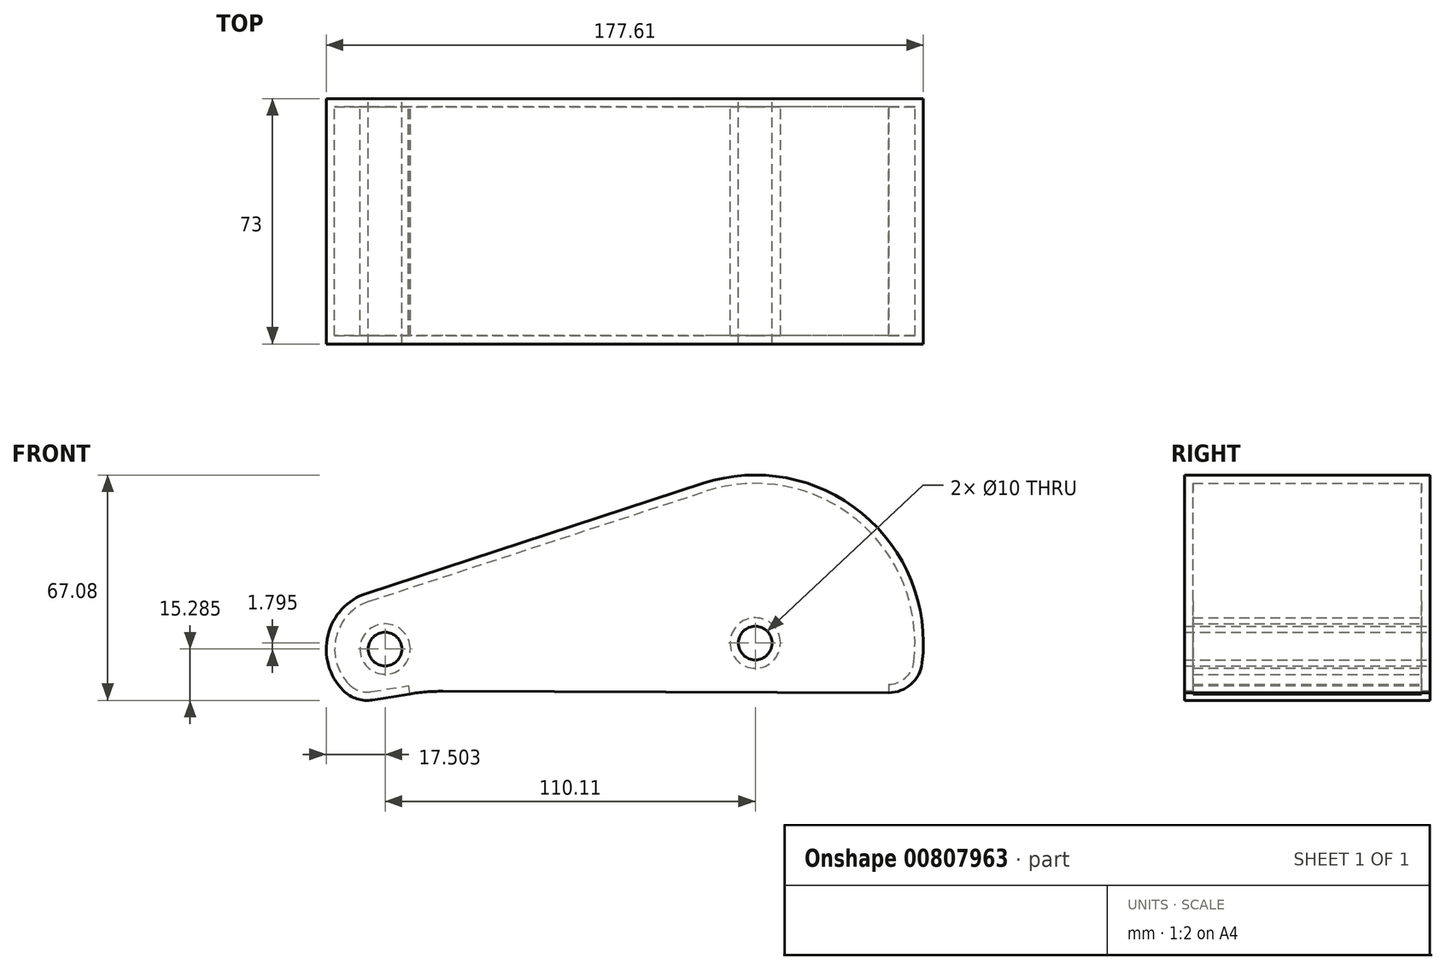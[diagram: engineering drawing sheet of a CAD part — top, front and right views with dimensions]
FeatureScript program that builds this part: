
annotation { "Feature Type Name" : "Feature", "Feature Type Description" : "" }
export const myFeature = defineFeature(function(context is Context, id is Id, definition is map)
    precondition{}
    {
        {
            var Q0;
            Q0=qCreatedBy(makeId("Front.planeOp"),FACE);
            var sketch = newSketch(context, id + "F0", { "sketchPlane" : qUnion([Q0])});
            skPoint(sketch, "E0.third.point", {"position": v(77.43, -43.66) * mm});
            skArc(sketch, "E1", {"start": v(110.72, -2.18) * mm, "mid": v(98.04, 48.25) * mm, "end": v(47.43, 60.15) * mm});
            skCircle(sketch, "E2", {"center": v(62.96, 12.62) * mm, "radius": 5 * mm});
            skCircle(sketch, "E3", {"center": v(-47.15, 10.82) * mm, "radius": 5 * mm});
            skCircle(sketch, "E4", {"center": v(62.96, 12.62) * mm, "radius": 45 * mm});
            skLineSegment(sketch, "E5", {"start": v(20.38, -1.92) * mm, "end": v(110.72, -2.18) * mm});
            skLineSegment(sketch, "E6", {"start": v(110.72, -2.18) * mm, "end": v(-34.94, -1.71) * mm});
            skArc(sketch, "E7", {"start": v(-52.58, 27.46) * mm, "mid": v(-64.6, 11.97) * mm, "end": v(-54.7, -4.96) * mm});
            skLineSegment(sketch, "E8", {"start": v(-52.58, 27.46) * mm, "end": v(47.43, 60.15) * mm});
            skLineSegment(sketch, "E9", {"start": v(-54.7, -4.96) * mm, "end": v(-34.94, -1.71) * mm});
            skSolve(sketch);
        }
        {
            var Q0;
            {var subQ0=sQuery(id+"F0.wireOp",EDGE,"E1");Q0=makeQuery(id+"F0.imprint","IMPRINT",FACE,{"disambiguationData":[TD([[makeQuery(id+"F0.imprint","IMPRINT",EDGE,{"derivedFrom":subQ0}),1.0]])]});}
            var Q1;
            Q1=makeQuery(id+"F0.imprint","IMPRINT",FACE,{"disambiguationData":[TD([[makeQuery(id+"F0.imprint","IMPRINT",EDGE,{"derivedFrom":sQuery(id+"F0.wireOp",EDGE,"E2")}),-1.0]])]});
            extrude(context, id + "F1", {"entities" : qUnion([Q0, Q1]), "depth" : 73 * mm, "offsetDistance" : 25 * mm});
        }
        {
            var Q0;
            Q0=makeQuery(id+"F1.opExtrude","SWEPT_EDGE",EDGE,{"disambiguationData":[OSD([sQuery(id+"F0.wireOp",EDGE,"E6"),sQuery(id+"F0.wireOp",EDGE,"E9")])]});
            fillet(context, id + "F2", {"entities" : qUnion([Q0]), "radius" : 60 * mm, "tangentPropagation" : true, "rho" : 0.5, "crossSection" : FilletCrossSection.CONIC, "allowEdgeOverflow" : false});
        }
        {
            var Q0;
            Q0=makeQuery(id+"F1.opExtrude","SWEPT_EDGE",EDGE,{"disambiguationData":[OSD([sQuery(id+"F0.wireOp",EDGE,"E1"),sQuery(id+"F0.wireOp",EDGE,"E5"),sQuery(id+"F0.wireOp",EDGE,"E6")])]});
            var Q1;
            Q1=makeQuery(id+"F1.opExtrude","SWEPT_EDGE",EDGE,{"disambiguationData":[OSD([sQuery(id+"F0.wireOp",EDGE,"E7"),sQuery(id+"F0.wireOp",EDGE,"E9")])]});
            fillet(context, id + "F3", {"entities" : qUnion([Q0, Q1]), "radius" : 10 * mm, "tangentPropagation" : true, "allowEdgeOverflow" : false});
        }
        {
            var Q0;
            Q0=makeQuery(id+"F1.opExtrude","SWEPT_FACE",FACE,{"disambiguationData":[OSD([sQuery(id+"F0.wireOp",EDGE,"E6")])]});
            var Q1;
            Q1=makeQuery(id+"F2.opFillet","BLEND_FACE",FACE,{"disambiguationData":[OSD([sQuery(id+"F0.wireOp",EDGE,"E6"),sQuery(id+"F0.wireOp",EDGE,"E7")])]});
            shell(context, id + "F4", {"entities" : qUnion([Q0, Q1]), "thickness" : 2.5 * mm});
        }
    });
